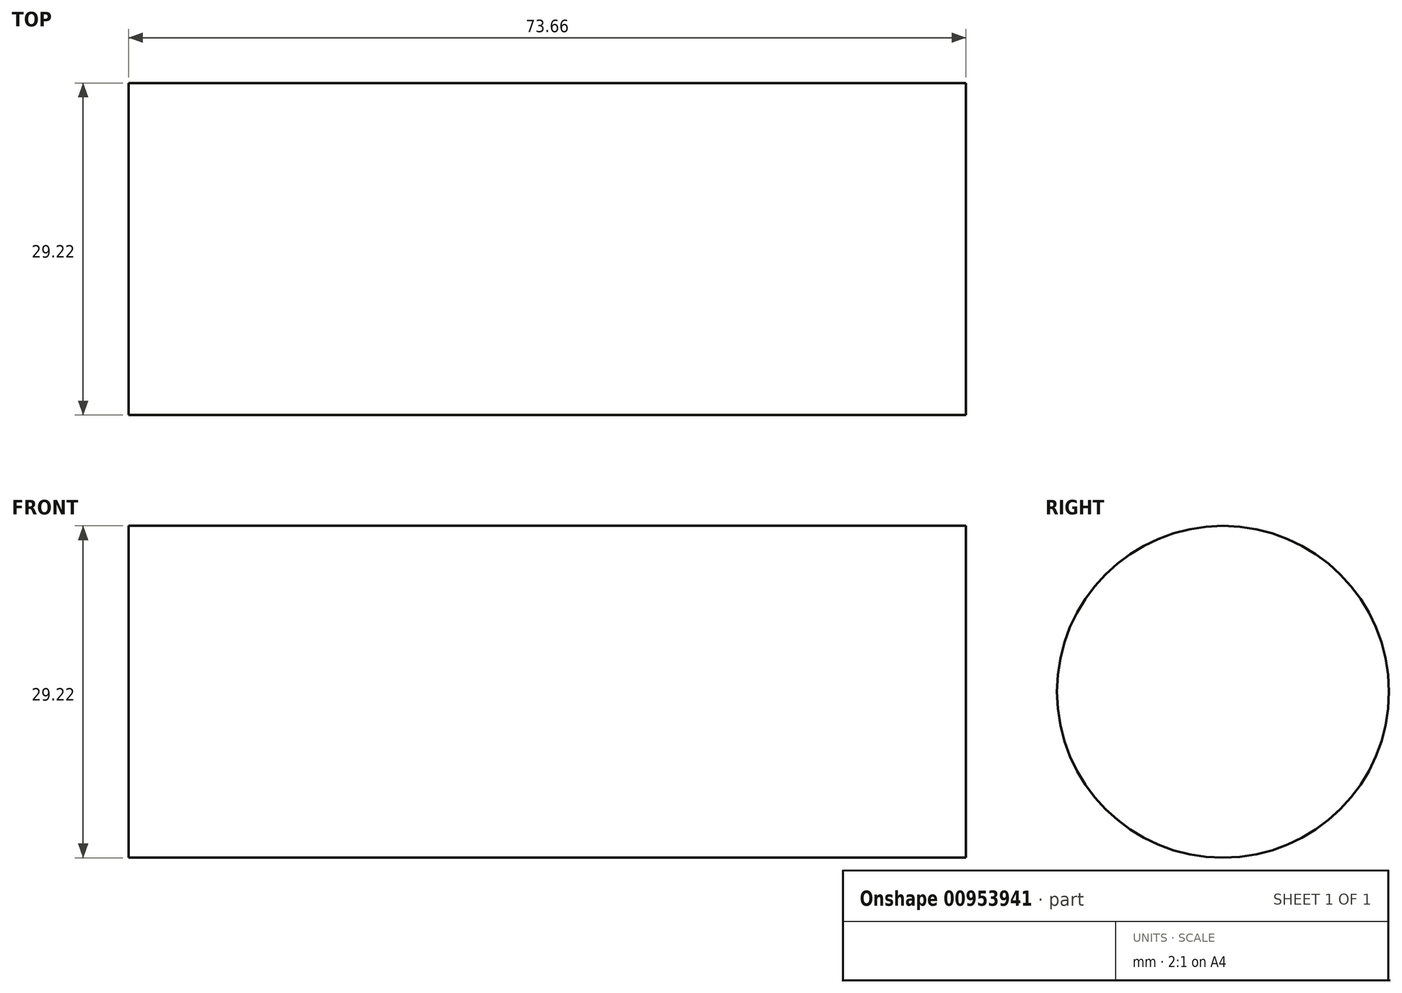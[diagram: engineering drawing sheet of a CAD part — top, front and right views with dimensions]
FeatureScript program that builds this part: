
annotation { "Feature Type Name" : "Feature", "Feature Type Description" : "" }
export const myFeature = defineFeature(function(context is Context, id is Id, definition is map)
    precondition{}
    {
        {
            var Q0;
            Q0=qCreatedBy(makeId("Top.planeOp"),FACE);
            var sketch = newSketch(context, id + "F0", { "sketchPlane" : qUnion([Q0])});
            skLineSegment(sketch, "E0", {"start": v(0, 0) * mm, "end": v(46.42, 0) * mm});
            skLineSegment(sketch, "E1", {"start": v(46.42, 0) * mm, "end": v(46.42, 14.6) * mm});
            skLineSegment(sketch, "E2", {"start": v(46.42, 14.6) * mm, "end": v(-27.24, 14.6) * mm});
            skLineSegment(sketch, "E3", {"start": v(-27.24, 14.6) * mm, "end": v(-27.24, 0) * mm});
            skLineSegment(sketch, "E4", {"start": v(-27.24, 0) * mm, "end": v(0, 0) * mm});
            skSolve(sketch);
        }
        {
            var Q0;
            Q0=makeQuery(id+"F0.imprint","IMPRINT",FACE,{"disambiguationData":[TD([[makeQuery(id+"F0.imprint","IMPRINT",EDGE,{"derivedFrom":sQuery(id+"F0.wireOp",EDGE,"E0")}),1.0]])]});
            var Q1;
            Q1=sQuery(id+"F0.wireOp",EDGE,"E4");
            revolve(context, id + "F1", {"surfaceOperationType" : NewSurfaceOperationType.NEW, "entities" : qUnion([Q0]), "axis" : qUnion([Q1]), "revolveType" : RevolveType.FULL});
        }
    });
